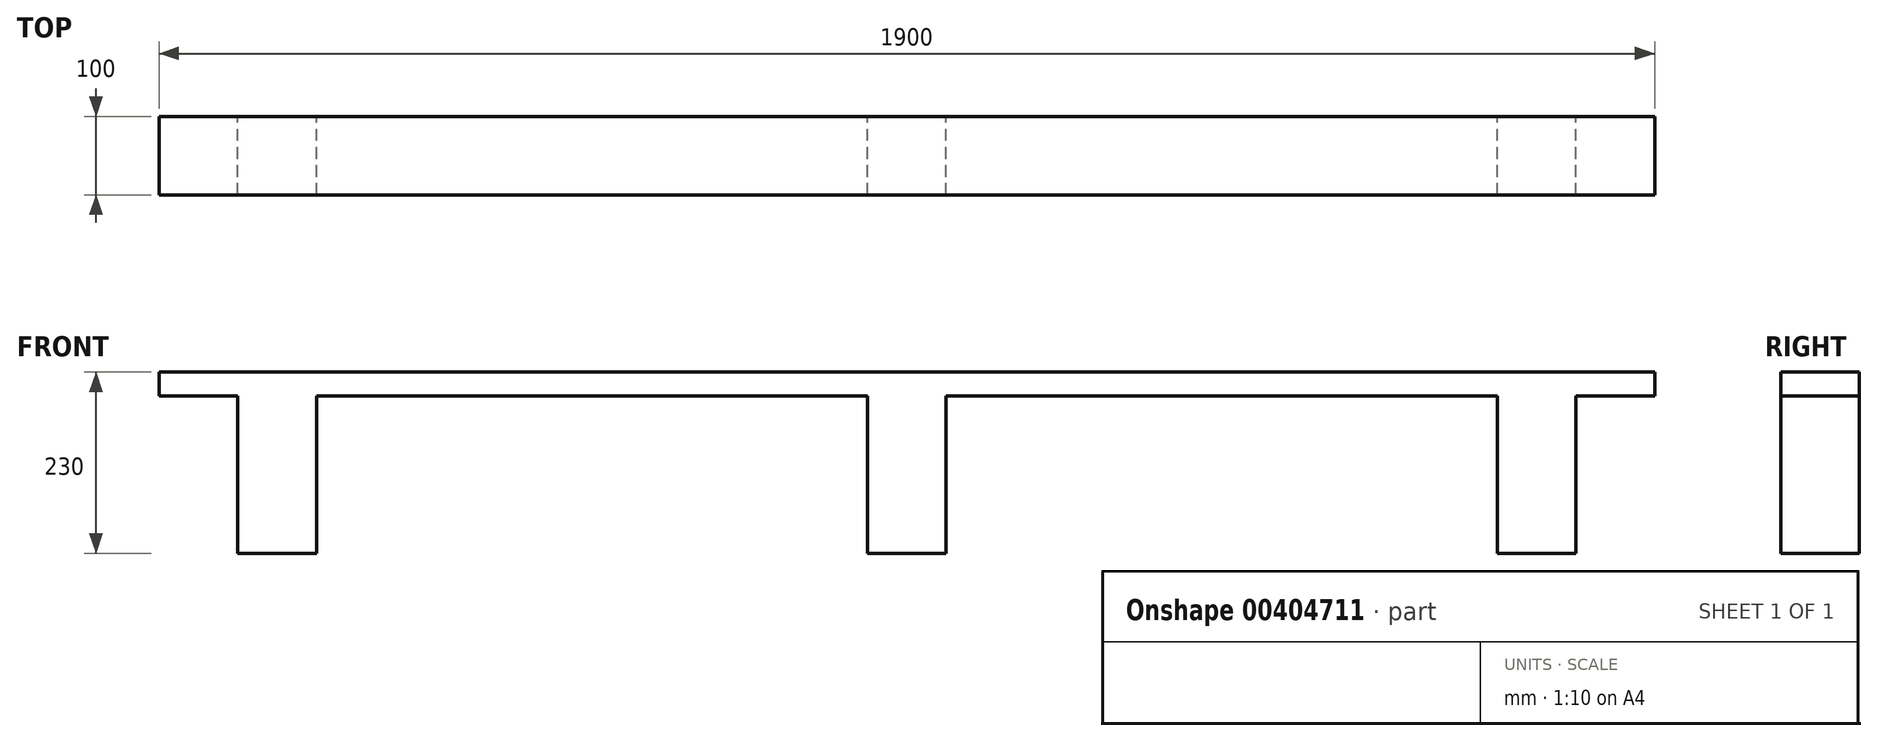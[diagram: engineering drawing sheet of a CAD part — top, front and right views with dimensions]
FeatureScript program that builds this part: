
annotation { "Feature Type Name" : "Feature", "Feature Type Description" : "" }
export const myFeature = defineFeature(function(context is Context, id is Id, definition is map)
    precondition{}
    {
        {
            var Q0;
            Q0=qCreatedBy(makeId("Front.planeOp"),FACE);
            var sketch = newSketch(context, id + "F0", { "sketchPlane" : qUnion([Q0])});
            skLineSegment(sketch, "E0.bottom", {"start": v(950, -15) * mm, "end": v(-950, -15) * mm});
            skLineSegment(sketch, "E0.top", {"start": v(950, 15) * mm, "end": v(-950, 15) * mm});
            skLineSegment(sketch, "E0.left", {"start": v(950, -15) * mm, "end": v(950, 15) * mm});
            skLineSegment(sketch, "E0.right", {"start": v(-950, -15) * mm, "end": v(-950, 15) * mm});
            skPoint(sketch, "E0.middle", {"position": v(0, 0) * mm});
            skLineSegment(sketch, "E1", {"start": v(-50, -15) * mm, "end": v(-50, -215) * mm});
            skLineSegment(sketch, "E2", {"start": v(-50, -215) * mm, "end": v(50, -215) * mm});
            skLineSegment(sketch, "E3", {"start": v(50, -215) * mm, "end": v(50, -15) * mm});
            skLineSegment(sketch, "E4", {"start": v(750, -15) * mm, "end": v(750, -215) * mm});
            skLineSegment(sketch, "E5", {"start": v(750, -215) * mm, "end": v(850, -215) * mm});
            skLineSegment(sketch, "E6", {"start": v(850, -215) * mm, "end": v(850, -15) * mm});
            skLineSegment(sketch, "E7", {"start": v(-850, -15) * mm, "end": v(-850, -215) * mm});
            skLineSegment(sketch, "E8", {"start": v(-850, -215) * mm, "end": v(-750, -215) * mm});
            skLineSegment(sketch, "E9", {"start": v(-750, -215) * mm, "end": v(-750, -15) * mm});
            skSolve(sketch);
        }
        {
            var Q0;
            Q0 = qSketchRegion(id + "F0", true);
            extrude(context, id + "F1", {"entities" : qUnion([Q0]), "depth" : 100 * mm});
        }
    });
